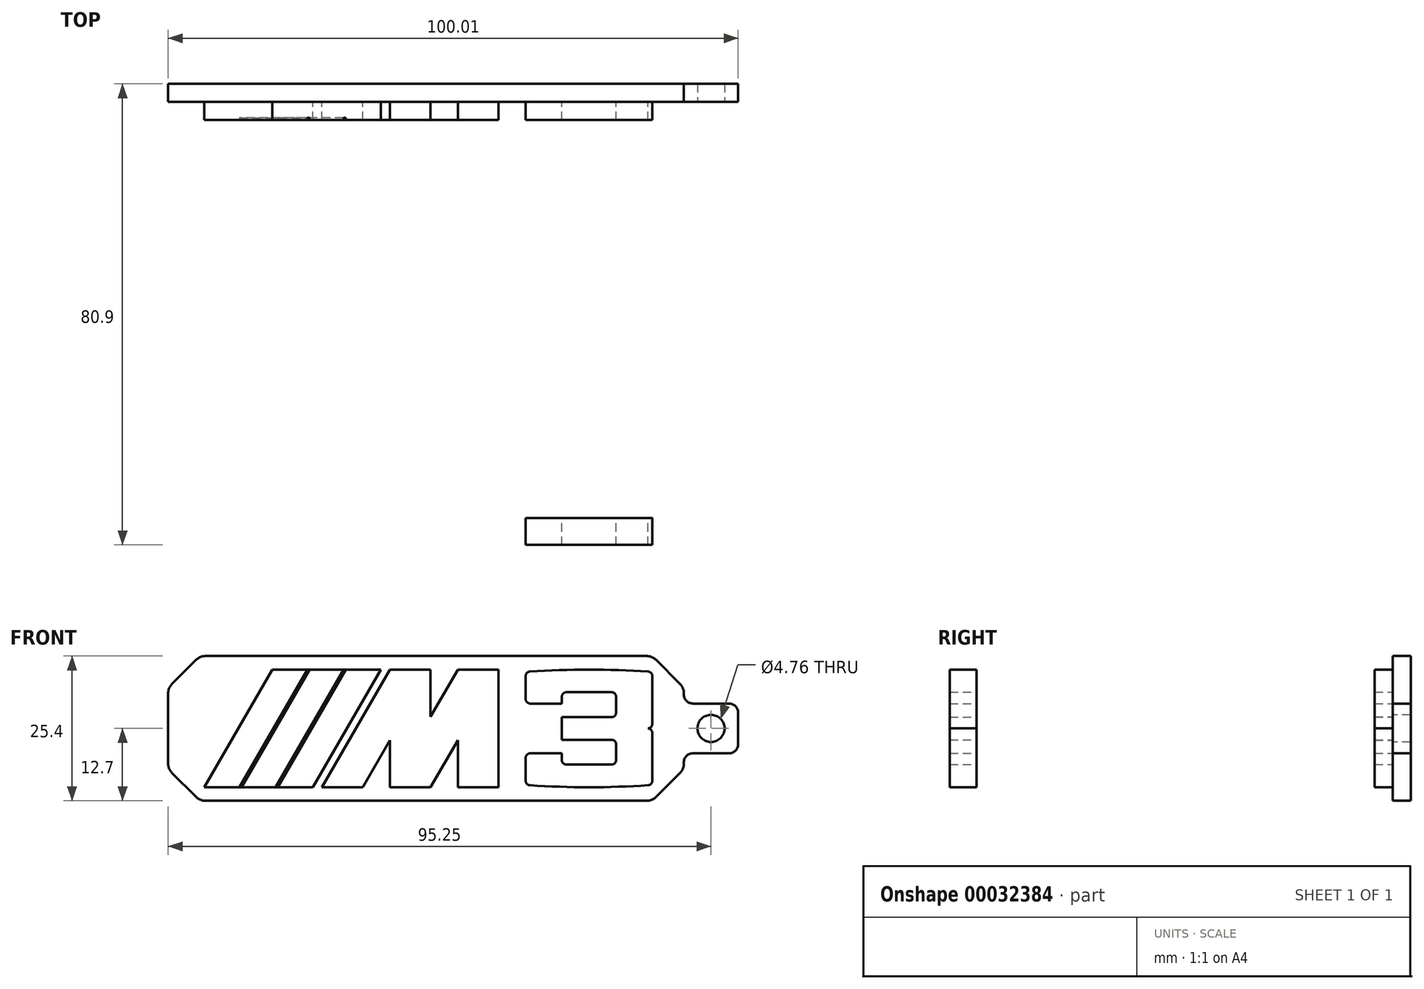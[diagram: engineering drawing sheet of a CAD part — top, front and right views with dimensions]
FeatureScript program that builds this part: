
annotation { "Feature Type Name" : "Feature", "Feature Type Description" : "" }
export const myFeature = defineFeature(function(context is Context, id is Id, definition is map)
    precondition{}
    {
        {
            var Q0;
            Q0=qCreatedBy(makeId("Front.planeOp"),FACE);
            var sketch = newSketch(context, id + "F0", { "sketchPlane" : qUnion([Q0])});
            skLineSegment(sketch, "E0.bottom", {"start": v(5.56, 0) * mm, "end": v(84.93, 0) * mm});
            skLineSegment(sketch, "E1", {"start": v(5.56, 25.4) * mm, "end": v(0, 19.84) * mm});
            skLineSegment(sketch, "E2", {"start": v(0, 5.56) * mm, "end": v(5.56, 0) * mm});
            skLineSegment(sketch, "E3", {"start": v(90.49, 12.7) * mm, "end": v(0, 12.7) * mm, "construction": true});
            skPoint(sketch, "E4.orphan", {"position": v(0, 25.4) * mm});
            skPoint(sketch, "E5.orphan", {"position": v(0, 0) * mm});
            skLineSegment(sketch, "E6", {"start": v(84.93, 25.4) * mm, "end": v(90.49, 19.84) * mm});
            skLineSegment(sketch, "E7", {"start": v(90.49, 19.84) * mm, "end": v(90.49, 5.56) * mm});
            skLineSegment(sketch, "E8", {"start": v(5.56, 25.4) * mm, "end": v(84.93, 25.4) * mm});
            skPoint(sketch, "E9.orphan", {"position": v(90.49, 25.4) * mm});
            skLineSegment(sketch, "E10", {"start": v(90.49, 5.56) * mm, "end": v(84.93, 0) * mm});
            skPoint(sketch, "E11.orphan", {"position": v(90.49, 0) * mm});
            skLineSegment(sketch, "E12.trimOffspring", {"start": v(0, 5.56) * mm, "end": v(0, 19.84) * mm});
            skSolve(sketch);
        }
        {
            var Q0;
            Q0=makeQuery(id+"F0.imprint","IMPRINT",FACE,{"disambiguationData":[TD([[makeQuery(id+"F0.imprint","IMPRINT",EDGE,{"derivedFrom":sQuery(id+"F0.wireOp",EDGE,"E0.bottom")}),1.0]])]});
            extrude(context, id + "F1", {"entities" : qUnion([Q0]), "depth" : 3.17 * mm});
        }
        {
            var Q0;
            Q0=makeQuery(id+"F1.opExtrude","CAP_FACE",FACE,{"disambiguationData":[OSD([sQuery(id+"F0.wireOp",EDGE,"E0.bottom"),sQuery(id+"F0.wireOp",EDGE,"E0.top"),sQuery(id+"F0.wireOp",EDGE,"E0.left"),sQuery(id+"F0.wireOp",EDGE,"E0.right")])],"isStart":false});
            var sketch = newSketch(context, id + "F2", { "sketchPlane" : qUnion([Q0])});
            skLineSegment(sketch, "E13", {"start": v(0, 2.38) * mm, "end": v(87.31, 2.38) * mm, "construction": true});
            skLineSegment(sketch, "E14", {"start": v(0, 23.02) * mm, "end": v(87.31, 23.02) * mm, "construction": true});
            skLineSegment(sketch, "E15", {"start": v(6.35, 2.38) * mm, "end": v(18.27, 23.02) * mm});
            skLineSegment(sketch, "E16", {"start": v(18.27, 23.02) * mm, "end": v(37.32, 23.02) * mm});
            skLineSegment(sketch, "E17", {"start": v(37.32, 23.02) * mm, "end": v(25.4, 2.38) * mm});
            skLineSegment(sketch, "E18", {"start": v(25.4, 2.38) * mm, "end": v(6.35, 2.38) * mm});
            skLineSegment(sketch, "E19", {"start": v(26.99, 2.38) * mm, "end": v(38.9, 23.02) * mm});
            skLineSegment(sketch, "E20", {"start": v(38.9, 23.02) * mm, "end": v(46.05, 23.02) * mm});
            skLineSegment(sketch, "E21", {"start": v(46.05, 23.02) * mm, "end": v(46.05, 14.75) * mm});
            skLineSegment(sketch, "E22", {"start": v(46.05, 14.75) * mm, "end": v(50.82, 23.02) * mm});
            skLineSegment(sketch, "E23", {"start": v(50.82, 23.02) * mm, "end": v(57.96, 23.02) * mm});
            skLineSegment(sketch, "E24", {"start": v(57.96, 23.02) * mm, "end": v(57.96, 2.38) * mm});
            skLineSegment(sketch, "E25", {"start": v(57.96, 2.38) * mm, "end": v(50.82, 2.38) * mm});
            skLineSegment(sketch, "E26", {"start": v(50.82, 2.38) * mm, "end": v(50.82, 10.65) * mm});
            skLineSegment(sketch, "E27", {"start": v(50.82, 10.65) * mm, "end": v(46.05, 2.38) * mm});
            skLineSegment(sketch, "E28", {"start": v(46.05, 2.38) * mm, "end": v(38.9, 2.38) * mm});
            skLineSegment(sketch, "E29", {"start": v(38.9, 2.38) * mm, "end": v(38.9, 10.65) * mm});
            skLineSegment(sketch, "E30", {"start": v(38.9, 10.65) * mm, "end": v(34.13, 2.38) * mm});
            skLineSegment(sketch, "E31", {"start": v(34.13, 2.38) * mm, "end": v(26.99, 2.38) * mm});
            skLineSegment(sketch, "E32.left", {"start": v(62.72, 21.88) * mm, "end": v(62.72, 17.86) * mm});
            skLineSegment(sketch, "E32.right", {"start": v(84.95, 21.88) * mm, "end": v(84.95, 16.87) * mm});
            skPoint(sketch, "E33.visualSharp", {"position": v(62.72, 23.02) * mm});
            skPoint(sketch, "E34.visualSharp", {"position": v(62.72, 2.38) * mm});
            skPoint(sketch, "E35.visualSharp", {"position": v(84.95, 2.38) * mm});
            skLineSegment(sketch, "E36", {"start": v(84.16, 23.02) * mm, "end": v(84.16, 2.38) * mm, "construction": true});
            skPoint(sketch, "E37", {"position": v(84.16, 12.7) * mm});
            skArc(sketch, "E38", {"start": v(84.16, 12.7) * mm, "mid": v(84.72, 12.93) * mm, "end": v(84.95, 13.5) * mm});
            skArc(sketch, "E39", {"start": v(84.95, 11.9) * mm, "mid": v(84.72, 12.47) * mm, "end": v(84.16, 12.7) * mm});
            skLineSegment(sketch, "E40", {"start": v(62.72, 12.7) * mm, "end": v(84.95, 12.7) * mm, "construction": true});
            skLineSegment(sketch, "E41", {"start": v(63.52, 17.07) * mm, "end": v(69.07, 17.07) * mm});
            skLineSegment(sketch, "E42", {"start": v(63.52, 8.33) * mm, "end": v(69.07, 8.33) * mm});
            skLineSegment(sketch, "E43", {"start": v(69.07, 17.07) * mm, "end": v(69.07, 18.26) * mm});
            skLineSegment(sketch, "E44", {"start": v(69.87, 19.05) * mm, "end": v(77.8, 19.05) * mm});
            skLineSegment(sketch, "E45", {"start": v(78.6, 18.26) * mm, "end": v(78.6, 15.48) * mm});
            skLineSegment(sketch, "E46", {"start": v(77.8, 14.68) * mm, "end": v(69.07, 14.68) * mm});
            skLineSegment(sketch, "E47", {"start": v(69.07, 14.68) * mm, "end": v(69.07, 10.72) * mm});
            skLineSegment(sketch, "E48", {"start": v(69.07, 10.72) * mm, "end": v(77.8, 10.72) * mm});
            skLineSegment(sketch, "E49", {"start": v(78.6, 9.92) * mm, "end": v(78.6, 7.14) * mm});
            skLineSegment(sketch, "E50", {"start": v(77.8, 6.35) * mm, "end": v(69.87, 6.35) * mm});
            skLineSegment(sketch, "E51", {"start": v(69.07, 7.14) * mm, "end": v(69.07, 8.33) * mm});
            skLineSegment(sketch, "E52", {"start": v(78.6, 16.87) * mm, "end": v(84.95, 16.87) * mm, "construction": true});
            skLineSegment(sketch, "E53.trimOffspring", {"start": v(62.72, 7.54) * mm, "end": v(62.72, 3.52) * mm});
            skArc(sketch, "E54", {"start": v(63.46, 2.73) * mm, "mid": v(73.84, 2.38) * mm, "end": v(84.2, 2.73) * mm});
            skArc(sketch, "E55", {"start": v(84.2, 22.67) * mm, "mid": v(73.84, 23.02) * mm, "end": v(63.46, 22.67) * mm});
            skPoint(sketch, "E56.visualSharp", {"position": v(84.95, 22.62) * mm});
            skArc(sketch, "E56.filletArc", {"start": v(84.95, 21.88) * mm, "mid": v(84.73, 22.42) * mm, "end": v(84.2, 22.67) * mm});
            skPoint(sketch, "E57.visualSharp", {"position": v(62.72, 22.62) * mm});
            skArc(sketch, "E57.filletArc", {"start": v(63.46, 22.67) * mm, "mid": v(62.94, 22.42) * mm, "end": v(62.72, 21.88) * mm});
            skPoint(sketch, "E58.visualSharp", {"position": v(62.72, 17.07) * mm});
            skArc(sketch, "E58.filletArc", {"start": v(62.72, 17.86) * mm, "mid": v(62.96, 17.3) * mm, "end": v(63.52, 17.07) * mm});
            skPoint(sketch, "E59.visualSharp", {"position": v(62.72, 8.33) * mm});
            skArc(sketch, "E59.filletArc", {"start": v(63.52, 8.33) * mm, "mid": v(62.96, 8.1) * mm, "end": v(62.72, 7.54) * mm});
            skPoint(sketch, "E60.visualSharp", {"position": v(62.72, 2.78) * mm});
            skArc(sketch, "E60.filletArc", {"start": v(62.72, 3.52) * mm, "mid": v(62.94, 2.98) * mm, "end": v(63.46, 2.73) * mm});
            skPoint(sketch, "E61.visualSharp", {"position": v(84.95, 2.78) * mm});
            skArc(sketch, "E61.filletArc", {"start": v(84.2, 2.73) * mm, "mid": v(84.73, 2.98) * mm, "end": v(84.95, 3.52) * mm});
            skPoint(sketch, "E62.visualSharp", {"position": v(69.07, 19.05) * mm});
            skArc(sketch, "E62.filletArc", {"start": v(69.87, 19.05) * mm, "mid": v(69.3, 18.82) * mm, "end": v(69.07, 18.26) * mm});
            skPoint(sketch, "E63.visualSharp", {"position": v(78.6, 19.05) * mm});
            skArc(sketch, "E63.filletArc", {"start": v(78.6, 18.26) * mm, "mid": v(78.37, 18.82) * mm, "end": v(77.8, 19.05) * mm});
            skPoint(sketch, "E64.visualSharp", {"position": v(78.6, 14.68) * mm});
            skArc(sketch, "E64.filletArc", {"start": v(77.8, 14.68) * mm, "mid": v(78.37, 14.92) * mm, "end": v(78.6, 15.48) * mm});
            skPoint(sketch, "E65.visualSharp", {"position": v(78.6, 10.72) * mm});
            skArc(sketch, "E65.filletArc", {"start": v(78.6, 9.92) * mm, "mid": v(78.37, 10.48) * mm, "end": v(77.8, 10.72) * mm});
            skPoint(sketch, "E66.visualSharp", {"position": v(78.6, 6.35) * mm});
            skArc(sketch, "E66.filletArc", {"start": v(77.8, 6.35) * mm, "mid": v(78.37, 6.58) * mm, "end": v(78.6, 7.14) * mm});
            skPoint(sketch, "E67.visualSharp", {"position": v(69.07, 6.35) * mm});
            skArc(sketch, "E67.filletArc", {"start": v(69.07, 7.14) * mm, "mid": v(69.3, 6.58) * mm, "end": v(69.87, 6.35) * mm});
            skLineSegment(sketch, "E68", {"start": v(62.72, 12.7) * mm, "end": v(69.07, 12.7) * mm, "construction": true});
            skLineSegment(sketch, "E69.trimOffspring", {"start": v(84.95, 11.9) * mm, "end": v(84.95, 3.52) * mm});
            skLineSegment(sketch, "E70", {"start": v(84.95, 16.87) * mm, "end": v(84.95, 13.5) * mm});
            skSolve(sketch);
        }
        {
            var Q0;
            Q0=qSketchRegion(id+"F2",true);
            extrude(context, id + "F3", {"entities" : qUnion([Q0]), "operationType" : NewBodyOperationType.ADD, "depth" : 3.17 * mm});
        }
        {
            var Q0;
            Q0=makeQuery(id+"F3.opExtrude","CAP_FACE",FACE,{"disambiguationData":[OSD([sQuery(id+"F2.wireOp",EDGE,"E15"),sQuery(id+"F2.wireOp",EDGE,"E16"),sQuery(id+"F2.wireOp",EDGE,"E17"),sQuery(id+"F2.wireOp",EDGE,"E18")])],"isStart":false});
            var sketch = newSketch(context, id + "F4", { "sketchPlane" : qUnion([Q0])});
            skLineSegment(sketch, "E71", {"start": v(24.62, 23.02) * mm, "end": v(12.7, 2.38) * mm, "construction": true});
            skLineSegment(sketch, "E72", {"start": v(30.97, 23.02) * mm, "end": v(19.05, 2.38) * mm, "construction": true});
            skLineSegment(sketch, "E73", {"start": v(12.3, 12.7) * mm, "end": v(18.66, 12.7) * mm, "construction": true});
            skLineSegment(sketch, "E74", {"start": v(18.66, 12.7) * mm, "end": v(25, 12.7) * mm, "construction": true});
            skLineSegment(sketch, "E75", {"start": v(25, 12.7) * mm, "end": v(31.36, 12.7) * mm, "construction": true});
            skLineSegment(sketch, "E76", {"start": v(31.16, 23.02) * mm, "end": v(19.25, 2.38) * mm});
            skLineSegment(sketch, "E77", {"start": v(30.77, 23.02) * mm, "end": v(18.85, 2.38) * mm});
            skLineSegment(sketch, "E78", {"start": v(30.77, 23.02) * mm, "end": v(31.16, 23.02) * mm});
            skLineSegment(sketch, "E79", {"start": v(18.85, 2.38) * mm, "end": v(19.25, 2.38) * mm});
            skLineSegment(sketch, "E80", {"start": v(24.81, 23.02) * mm, "end": v(12.9, 2.38) * mm});
            skLineSegment(sketch, "E81", {"start": v(12.9, 2.38) * mm, "end": v(12.5, 2.38) * mm});
            skLineSegment(sketch, "E82", {"start": v(12.5, 2.38) * mm, "end": v(24.42, 23.02) * mm});
            skLineSegment(sketch, "E83", {"start": v(24.42, 23.02) * mm, "end": v(24.81, 23.02) * mm});
            skSolve(sketch);
        }
        {
            var Q0;
            Q0=qSketchRegion(id+"F4",true);
            extrude(context, id + "F5", {"entities" : qUnion([Q0]), "operationType" : NewBodyOperationType.REMOVE, "oppositeDirection" : true, "depth" : 0.4 * mm});
        }
        {
            var Q0;
            Q0=makeQuery(id+"F1.opExtrude","SWEPT_EDGE",EDGE,{"disambiguationData":[OSD([sQuery(id+"F0.wireOp",EDGE,"E7"),sQuery(id+"F0.wireOp",EDGE,"6dd972b2-0395-4e63-bd1b-42e2af5a4723")])]});
            var Q1;
            Q1=makeQuery(id+"F1.opExtrude","SWEPT_EDGE",EDGE,{"disambiguationData":[OSD([sQuery(id+"F0.wireOp",EDGE,"E0.right"),sQuery(id+"F0.wireOp",EDGE,"6dd972b2-0395-4e63-bd1b-42e2af5a4723")])]});
            var Q2;
            Q2=makeQuery(id+"F1.opExtrude","SWEPT_EDGE",EDGE,{"disambiguationData":[OSD([sQuery(id+"F0.wireOp",EDGE,"E0.bottom"),sQuery(id+"F0.wireOp",EDGE,"E0.right")])]});
            var Q3;
            Q3=makeQuery(id+"F1.opExtrude","SWEPT_EDGE",EDGE,{"disambiguationData":[OSD([sQuery(id+"F0.wireOp",EDGE,"E6"),sQuery(id+"F0.wireOp",EDGE,"E7")])]});
            var Q4;
            Q4=makeQuery(id+"F1.opExtrude","SWEPT_EDGE",EDGE,{"disambiguationData":[OSD([sQuery(id+"F0.wireOp",EDGE,"E6"),sQuery(id+"F0.wireOp",EDGE,"E8")])]});
            var Q5;
            Q5=makeQuery(id+"F1.opExtrude","SWEPT_EDGE",EDGE,{"disambiguationData":[OSD([sQuery(id+"F0.wireOp",EDGE,"E1"),sQuery(id+"F0.wireOp",EDGE,"E8")])]});
            var Q6;
            Q6=makeQuery(id+"F1.opExtrude","SWEPT_EDGE",EDGE,{"disambiguationData":[OSD([sQuery(id+"F0.wireOp",EDGE,"E0.left"),sQuery(id+"F0.wireOp",EDGE,"E1")])]});
            var Q7;
            Q7=makeQuery(id+"F1.opExtrude","SWEPT_EDGE",EDGE,{"disambiguationData":[OSD([sQuery(id+"F0.wireOp",EDGE,"E0.left"),sQuery(id+"F0.wireOp",EDGE,"E2")])]});
            var Q8;
            Q8=makeQuery(id+"F1.opExtrude","SWEPT_EDGE",EDGE,{"disambiguationData":[OSD([sQuery(id+"F0.wireOp",EDGE,"E0.bottom"),sQuery(id+"F0.wireOp",EDGE,"E2")])]});
            var Q9;
            Q9=makeQuery(id+"F1.opExtrude","SWEPT_EDGE",EDGE,{"disambiguationData":[OSD([sQuery(id+"F0.wireOp",EDGE,"b47ece28-6d20-492b-9bea-9b02787d052c"),sQuery(id+"F0.wireOp",EDGE,"E12.trimOffspring")])]});
            var Q10;
            Q10=makeQuery(id+"F1.opExtrude","SWEPT_EDGE",EDGE,{"disambiguationData":[OSD([sQuery(id+"F0.wireOp",EDGE,"b47ece28-6d20-492b-9bea-9b02787d052c"),sQuery(id+"F0.wireOp",EDGE,"043795f3-4b57-43bd-8b6d-993c27947321")])]});
            var Q11;
            Q11=makeQuery(id+"F1.opExtrude","SWEPT_EDGE",EDGE,{"disambiguationData":[OSD([sQuery(id+"F0.wireOp",EDGE,"043795f3-4b57-43bd-8b6d-993c27947321"),sQuery(id+"F0.wireOp",EDGE,"06755655-8e5e-49be-bf8c-733d95aec83b")])]});
            fillet(context, id + "F6", {"entities" : qUnion([Q0, Q1, Q2, Q3, Q4, Q5, Q6, Q7, Q8, Q9, Q10, Q11]), "radius" : 2.38 * mm, "tangentPropagation" : true, "allowEdgeOverflow" : false});
        }
        {
            var Q0;
            Q0=makeQuery(id+"F1.opExtrude","CAP_FACE",FACE,{"disambiguationData":[OSD([sQuery(id+"F0.wireOp",EDGE,"E0.bottom"),sQuery(id+"F0.wireOp",EDGE,"E1"),sQuery(id+"F0.wireOp",EDGE,"E2"),sQuery(id+"F0.wireOp",EDGE,"E6"),sQuery(id+"F0.wireOp",EDGE,"E7"),sQuery(id+"F0.wireOp",EDGE,"E8"),sQuery(id+"F0.wireOp",EDGE,"E10"),sQuery(id+"F0.wireOp",EDGE,"E12.trimOffspring")])],"isStart":false});
            var sketch = newSketch(context, id + "F7", { "sketchPlane" : qUnion([Q0])});
            skLineSegment(sketch, "E84", {"start": v(0, 12.7) * mm, "end": v(90.49, 12.7) * mm, "construction": true});
            skLineSegment(sketch, "E85", {"start": v(45.24, 25.4) * mm, "end": v(45.24, 0) * mm, "construction": true});
            skLineSegment(sketch, "E86", {"start": v(100.01, 9.92) * mm, "end": v(100.01, 15.48) * mm});
            skLineSegment(sketch, "E87", {"start": v(98.43, 17.07) * mm, "end": v(92.08, 17.07) * mm});
            skCircle(sketch, "E88", {"center": v(95.25, 12.7) * mm, "radius": 2.38 * mm});
            skLineSegment(sketch, "E89", {"start": v(90.49, 18.65) * mm, "end": v(90.49, 6.75) * mm});
            skLineSegment(sketch, "E90", {"start": v(98.43, 8.33) * mm, "end": v(92.08, 8.33) * mm});
            skArc(sketch, "E91", {"start": v(92.08, 17.07) * mm, "mid": v(90.95, 17.53) * mm, "end": v(90.49, 18.65) * mm});
            skArc(sketch, "E92", {"start": v(92.08, 8.33) * mm, "mid": v(90.95, 7.87) * mm, "end": v(90.49, 6.75) * mm});
            skPoint(sketch, "E93.visualSharp", {"position": v(100.01, 17.07) * mm});
            skArc(sketch, "E93.filletArc", {"start": v(100.01, 15.48) * mm, "mid": v(99.55, 16.6) * mm, "end": v(98.43, 17.07) * mm});
            skPoint(sketch, "E94.visualSharp", {"position": v(100.01, 8.33) * mm});
            skArc(sketch, "E94.filletArc", {"start": v(98.43, 8.33) * mm, "mid": v(99.55, 8.8) * mm, "end": v(100.01, 9.92) * mm});
            skLineSegment(sketch, "E95.MirrorCS", {"start": v(-9.53, 9.92) * mm, "end": v(-9.53, 15.48) * mm, "construction": true});
            skCircle(sketch, "E96.MirrorC", {"center": v(-4.76, 12.7) * mm, "radius": 2.38 * mm, "construction": true});
            skLineSegment(sketch, "E97.MirrorCS", {"start": v(0, 18.65) * mm, "end": v(0, 6.75) * mm, "construction": true});
            skArc(sketch, "E98.MirrorCS", {"start": v(-1.59, 17.07) * mm, "mid": v(-0.46, 17.53) * mm, "end": v(0, 18.65) * mm, "construction": true});
            skArc(sketch, "E99.MirrorCS", {"start": v(-7.94, 8.33) * mm, "mid": v(-9.06, 8.8) * mm, "end": v(-9.53, 9.92) * mm, "construction": true});
            skLineSegment(sketch, "E100.MirrorCS", {"start": v(-7.94, 8.33) * mm, "end": v(-1.59, 8.33) * mm, "construction": true});
            skLineSegment(sketch, "E101.MirrorCS", {"start": v(-7.94, 17.07) * mm, "end": v(-1.59, 17.07) * mm, "construction": true});
            skArc(sketch, "E102.MirrorCS", {"start": v(-1.59, 8.33) * mm, "mid": v(-0.46, 7.87) * mm, "end": v(0, 6.75) * mm, "construction": true});
            skArc(sketch, "E103.MirrorCS", {"start": v(-9.53, 15.48) * mm, "mid": v(-9.06, 16.6) * mm, "end": v(-7.94, 17.07) * mm, "construction": true});
            skPoint(sketch, "E104.MirrorP", {"position": v(-9.53, 8.33) * mm});
            skPoint(sketch, "E105.MirrorP", {"position": v(-9.53, 17.07) * mm});
            skSolve(sketch);
        }
        {
            var Q0;
            Q0 = qSketchRegion(id + "F7", true);
            var Q1;
            Q1=makeQuery(id+"F1.opExtrude","CAP_FACE",FACE,{"disambiguationData":[OSD([sQuery(id+"F0.wireOp",EDGE,"E0.bottom"),sQuery(id+"F0.wireOp",EDGE,"E1"),sQuery(id+"F0.wireOp",EDGE,"E2"),sQuery(id+"F0.wireOp",EDGE,"E6"),sQuery(id+"F0.wireOp",EDGE,"E7"),sQuery(id+"F0.wireOp",EDGE,"E8"),sQuery(id+"F0.wireOp",EDGE,"E10"),sQuery(id+"F0.wireOp",EDGE,"E12.trimOffspring")])],"isStart":true});
            extrude(context, id + "F8", {"entities" : qUnion([Q0]), "operationType" : NewBodyOperationType.ADD, "endBound" : BoundingType.UP_TO_SURFACE, "oppositeDirection" : true, "endBoundEntityFace" : qUnion([Q1]), "depth" : 25.4 * mm});
        }
        {
            var Q0;
            Q0=qCreatedBy(makeId("Front.planeOp"),FACE);
            cPlane(context, id + "F9", {"entities" : qUnion([Q0]), "cplaneType" : CPlaneType.OFFSET, "offset" : 76.2 * mm, "width" : 152.4 * mm, "height" : 152.4 * mm});
        }
        {
            var Q0;
            Q0=qCreatedBy(id+"F9.planeOp",FACE);
            var sketch = newSketch(context, id + "F10", { "sketchPlane" : qUnion([Q0])});
            skLineSegment(sketch, "E106.0", {"start": v(0, 2.38) * mm, "end": v(87.31, 2.38) * mm, "construction": true});
            skLineSegment(sketch, "E106.1", {"start": v(0, 23.02) * mm, "end": v(87.31, 23.02) * mm, "construction": true});
            skLineSegment(sketch, "E106.2", {"start": v(6.35, 2.38) * mm, "end": v(18.27, 23.02) * mm, "construction": true});
            skLineSegment(sketch, "E106.3", {"start": v(18.27, 23.02) * mm, "end": v(37.32, 23.02) * mm, "construction": true});
            skLineSegment(sketch, "E106.4", {"start": v(37.32, 23.02) * mm, "end": v(25.4, 2.38) * mm, "construction": true});
            skLineSegment(sketch, "E106.5", {"start": v(25.4, 2.38) * mm, "end": v(6.35, 2.38) * mm, "construction": true});
            skLineSegment(sketch, "E106.6", {"start": v(26.99, 2.38) * mm, "end": v(38.9, 23.02) * mm, "construction": true});
            skLineSegment(sketch, "E106.7", {"start": v(38.9, 23.02) * mm, "end": v(46.05, 23.02) * mm, "construction": true});
            skLineSegment(sketch, "E106.8", {"start": v(46.05, 23.02) * mm, "end": v(46.05, 14.75) * mm, "construction": true});
            skLineSegment(sketch, "E106.9", {"start": v(46.05, 14.75) * mm, "end": v(50.82, 23.02) * mm, "construction": true});
            skLineSegment(sketch, "E106.10", {"start": v(50.82, 23.02) * mm, "end": v(57.96, 23.02) * mm, "construction": true});
            skLineSegment(sketch, "E106.11", {"start": v(57.96, 23.02) * mm, "end": v(57.96, 2.38) * mm, "construction": true});
            skLineSegment(sketch, "E106.12", {"start": v(57.96, 2.38) * mm, "end": v(50.82, 2.38) * mm, "construction": true});
            skLineSegment(sketch, "E106.13", {"start": v(50.82, 2.38) * mm, "end": v(50.82, 10.65) * mm, "construction": true});
            skLineSegment(sketch, "E106.14", {"start": v(50.82, 10.65) * mm, "end": v(46.05, 2.38) * mm, "construction": true});
            skLineSegment(sketch, "E106.15", {"start": v(46.05, 2.38) * mm, "end": v(38.9, 2.38) * mm, "construction": true});
            skLineSegment(sketch, "E106.16", {"start": v(38.9, 2.38) * mm, "end": v(38.9, 10.65) * mm, "construction": true});
            skLineSegment(sketch, "E106.17", {"start": v(38.9, 10.65) * mm, "end": v(34.13, 2.38) * mm, "construction": true});
            skLineSegment(sketch, "E106.18", {"start": v(34.13, 2.38) * mm, "end": v(26.99, 2.38) * mm, "construction": true});
            skLineSegment(sketch, "E106.19", {"start": v(62.72, 21.88) * mm, "end": v(62.72, 17.86) * mm});
            skLineSegment(sketch, "E106.20", {"start": v(84.95, 21.88) * mm, "end": v(84.95, 16.87) * mm});
            skPoint(sketch, "E106.21", {"position": v(62.72, 23.02) * mm});
            skPoint(sketch, "E106.22", {"position": v(62.72, 2.38) * mm});
            skPoint(sketch, "E106.23", {"position": v(84.95, 2.38) * mm});
            skLineSegment(sketch, "E106.24", {"start": v(84.16, 23.02) * mm, "end": v(84.16, 2.38) * mm, "construction": true});
            skPoint(sketch, "E106.25", {"position": v(84.16, 12.7) * mm});
            skArc(sketch, "E106.26", {"start": v(84.16, 12.7) * mm, "mid": v(84.72, 12.93) * mm, "end": v(84.95, 13.5) * mm});
            skArc(sketch, "E106.27", {"start": v(84.95, 11.9) * mm, "mid": v(84.72, 12.47) * mm, "end": v(84.16, 12.7) * mm});
            skLineSegment(sketch, "E106.28", {"start": v(62.72, 12.7) * mm, "end": v(84.95, 12.7) * mm, "construction": true});
            skLineSegment(sketch, "E106.29", {"start": v(63.52, 17.07) * mm, "end": v(69.07, 17.07) * mm});
            skLineSegment(sketch, "E106.30", {"start": v(63.52, 8.33) * mm, "end": v(69.07, 8.33) * mm});
            skLineSegment(sketch, "E106.31", {"start": v(69.07, 17.07) * mm, "end": v(69.07, 18.26) * mm});
            skLineSegment(sketch, "E106.32", {"start": v(69.87, 19.05) * mm, "end": v(77.8, 19.05) * mm});
            skLineSegment(sketch, "E106.33", {"start": v(78.6, 18.26) * mm, "end": v(78.6, 15.48) * mm});
            skLineSegment(sketch, "E106.34", {"start": v(77.8, 14.68) * mm, "end": v(69.07, 14.68) * mm});
            skLineSegment(sketch, "E106.35", {"start": v(69.07, 14.68) * mm, "end": v(69.07, 10.72) * mm});
            skLineSegment(sketch, "E106.36", {"start": v(69.07, 10.72) * mm, "end": v(77.8, 10.72) * mm});
            skLineSegment(sketch, "E106.37", {"start": v(78.6, 9.92) * mm, "end": v(78.6, 7.14) * mm});
            skLineSegment(sketch, "E106.38", {"start": v(77.8, 6.35) * mm, "end": v(69.87, 6.35) * mm});
            skLineSegment(sketch, "E106.39", {"start": v(69.07, 7.14) * mm, "end": v(69.07, 8.33) * mm});
            skLineSegment(sketch, "E106.40", {"start": v(78.6, 16.87) * mm, "end": v(84.95, 16.87) * mm, "construction": true});
            skLineSegment(sketch, "E106.41", {"start": v(62.72, 7.54) * mm, "end": v(62.72, 3.52) * mm});
            skArc(sketch, "E106.42", {"start": v(63.46, 2.73) * mm, "mid": v(73.84, 2.38) * mm, "end": v(84.2, 2.73) * mm});
            skArc(sketch, "E106.43", {"start": v(84.2, 22.67) * mm, "mid": v(73.84, 23.02) * mm, "end": v(63.46, 22.67) * mm});
            skPoint(sketch, "E106.44", {"position": v(84.95, 22.62) * mm});
            skArc(sketch, "E106.45", {"start": v(84.95, 21.88) * mm, "mid": v(84.73, 22.42) * mm, "end": v(84.2, 22.67) * mm});
            skPoint(sketch, "E106.46", {"position": v(62.72, 22.62) * mm});
            skArc(sketch, "E106.47", {"start": v(63.46, 22.67) * mm, "mid": v(62.94, 22.42) * mm, "end": v(62.72, 21.88) * mm});
            skPoint(sketch, "E106.48", {"position": v(62.72, 17.07) * mm});
            skArc(sketch, "E106.49", {"start": v(62.72, 17.86) * mm, "mid": v(62.96, 17.3) * mm, "end": v(63.52, 17.07) * mm});
            skPoint(sketch, "E106.50", {"position": v(62.72, 8.33) * mm});
            skArc(sketch, "E106.51", {"start": v(63.52, 8.33) * mm, "mid": v(62.96, 8.1) * mm, "end": v(62.72, 7.54) * mm});
            skPoint(sketch, "E106.52", {"position": v(62.72, 2.78) * mm});
            skArc(sketch, "E106.53", {"start": v(62.72, 3.52) * mm, "mid": v(62.94, 2.98) * mm, "end": v(63.46, 2.73) * mm});
            skPoint(sketch, "E106.54", {"position": v(84.95, 2.78) * mm});
            skArc(sketch, "E106.55", {"start": v(84.2, 2.73) * mm, "mid": v(84.73, 2.98) * mm, "end": v(84.95, 3.52) * mm});
            skPoint(sketch, "E106.56", {"position": v(69.07, 19.05) * mm});
            skArc(sketch, "E106.57", {"start": v(69.87, 19.05) * mm, "mid": v(69.3, 18.82) * mm, "end": v(69.07, 18.26) * mm});
            skPoint(sketch, "E106.58", {"position": v(78.6, 19.05) * mm});
            skArc(sketch, "E106.59", {"start": v(78.6, 18.26) * mm, "mid": v(78.37, 18.82) * mm, "end": v(77.8, 19.05) * mm});
            skPoint(sketch, "E106.60", {"position": v(78.6, 14.68) * mm});
            skArc(sketch, "E106.61", {"start": v(77.8, 14.68) * mm, "mid": v(78.37, 14.92) * mm, "end": v(78.6, 15.48) * mm});
            skPoint(sketch, "E106.62", {"position": v(78.6, 10.72) * mm});
            skArc(sketch, "E106.63", {"start": v(78.6, 9.92) * mm, "mid": v(78.37, 10.48) * mm, "end": v(77.8, 10.72) * mm});
            skPoint(sketch, "E106.64", {"position": v(78.6, 6.35) * mm});
            skArc(sketch, "E106.65", {"start": v(77.8, 6.35) * mm, "mid": v(78.37, 6.58) * mm, "end": v(78.6, 7.14) * mm});
            skPoint(sketch, "E106.66", {"position": v(69.07, 6.35) * mm});
            skArc(sketch, "E106.67", {"start": v(69.07, 7.14) * mm, "mid": v(69.3, 6.58) * mm, "end": v(69.87, 6.35) * mm});
            skLineSegment(sketch, "E106.68", {"start": v(62.72, 12.7) * mm, "end": v(69.07, 12.7) * mm});
            skLineSegment(sketch, "E106.69", {"start": v(84.95, 11.9) * mm, "end": v(84.95, 3.52) * mm});
            skLineSegment(sketch, "E106.70", {"start": v(84.95, 16.87) * mm, "end": v(84.95, 13.5) * mm});
            skSolve(sketch);
        }
        {
            var Q0;
            Q0=makeQuery(id+"F10.imprint","IMPRINT",FACE,{"disambiguationData":[TD([[makeQuery(id+"F10.imprint","IMPRINT",EDGE,{"derivedFrom":sQuery(id+"F10.wireOp",EDGE,"E106.19")}),1.0]])]});
            var Q1;
            Q1=sQuery(id+"F10.wireOp",EDGE,"E106.24");
            var Q2;
            Q2=sQuery(id+"F10.wireOp",EDGE,"E106.40");
            var Q3;
            Q3=sQuery(id+"F10.wireOp",EDGE,"E106.28");
            extrude(context, id + "F11", {"entities" : qUnion([Q0]), "surfaceEntities" : qUnion([Q1, Q2, Q3]), "depth" : 3.17 * mm});
        }
        {
            var Q0;
            Q0=makeQuery(id+"F11.opExtrude","CAP_FACE",FACE,{"disambiguationData":[OSD([sQuery(id+"F10.wireOp",EDGE,"E106.19"),sQuery(id+"F10.wireOp",EDGE,"E106.20"),sQuery(id+"F10.wireOp",EDGE,"E106.26"),sQuery(id+"F10.wireOp",EDGE,"E106.27"),sQuery(id+"F10.wireOp",EDGE,"E106.29"),sQuery(id+"F10.wireOp",EDGE,"E106.30"),sQuery(id+"F10.wireOp",EDGE,"E106.31"),sQuery(id+"F10.wireOp",EDGE,"E106.32"),sQuery(id+"F10.wireOp",EDGE,"E106.33"),sQuery(id+"F10.wireOp",EDGE,"E106.34"),sQuery(id+"F10.wireOp",EDGE,"E106.35"),sQuery(id+"F10.wireOp",EDGE,"E106.36"),sQuery(id+"F10.wireOp",EDGE,"E106.37"),sQuery(id+"F10.wireOp",EDGE,"E106.38"),sQuery(id+"F10.wireOp",EDGE,"E106.39"),sQuery(id+"F10.wireOp",EDGE,"E106.41"),sQuery(id+"F10.wireOp",EDGE,"E106.42"),sQuery(id+"F10.wireOp",EDGE,"E106.43"),sQuery(id+"F10.wireOp",EDGE,"E106.45"),sQuery(id+"F10.wireOp",EDGE,"E106.47"),sQuery(id+"F10.wireOp",EDGE,"E106.49"),sQuery(id+"F10.wireOp",EDGE,"E106.51"),sQuery(id+"F10.wireOp",EDGE,"E106.53"),sQuery(id+"F10.wireOp",EDGE,"E106.55"),sQuery(id+"F10.wireOp",EDGE,"E106.57"),sQuery(id+"F10.wireOp",EDGE,"E106.59"),sQuery(id+"F10.wireOp",EDGE,"E106.61"),sQuery(id+"F10.wireOp",EDGE,"E106.63"),sQuery(id+"F10.wireOp",EDGE,"E106.65"),sQuery(id+"F10.wireOp",EDGE,"E106.67"),sQuery(id+"F10.wireOp",EDGE,"E106.69"),sQuery(id+"F10.wireOp",EDGE,"E106.70")])],"isStart":false});
            extrude(context, id + "F12", {"entities" : qUnion([Q0]), "operationType" : NewBodyOperationType.ADD, "depth" : 1.52 * mm});
        }
    });
